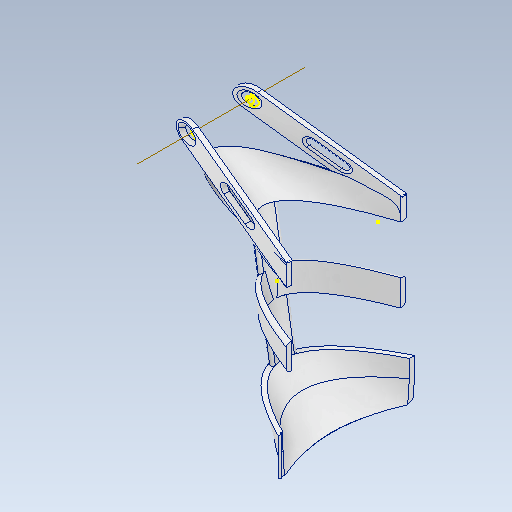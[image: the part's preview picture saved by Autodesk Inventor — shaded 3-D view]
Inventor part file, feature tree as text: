
AUTODESK INVENTOR PART (.ipt)
format: ipt  version: 2021 (Build 250183000, 183)  size: 1,121,280 bytes
history: native  units: mm
features: sketch x37, plane x11, other x4
ambient origin geometry x8: Origin, YZ Plane, XZ Plane, XY Plane, X Axis, Y Axis, Z Axis, Center Point
bodies: Solid1 (feature_tree)
feature tree (52):
  other  "Shoes (upper part).ipt"
  other  "Solid1::Shoes (upper part).ipt"
  other  "TaggingFeature1"
  sketch  "Sketch1"  dims[d0=10.0mm]
  sketch  "Sketch2"
  sketch  "Sketch3"
  sketch  "Sketch4"
  sketch  "Sketch5"
  sketch  "Sketch6"
  sketch  "Sketch7"
  sketch  "Sketch8"
  sketch  "Sketch9"
  sketch  "Sketch10"
  sketch  "Sketch11"
  sketch  "Sketch12"
  sketch  "Sketch13"
  sketch  "Sketch14"
  sketch  "Sketch15"
  sketch  "Sketch16"
  sketch  "Sketch17"
  sketch  "Sketch18"
  sketch  "Sketch19"
  sketch  "Sketch20"
  sketch  "Sketch21"
  sketch  "Sketch22"
  sketch  "Sketch23"
  sketch  "Sketch24"
  sketch  "Sketch25"
  sketch  "Sketch26"
  sketch  "Sketch27"
  sketch  "Sketch28"
  sketch  "Sketch29"
  sketch  "Sketch30"
  sketch  "Sketch31"
  sketch  "Sketch32"
  sketch  "Sketch33"
  sketch  "Sketch34"
  sketch  "Sketch35"
  sketch  "Sketch36"
  sketch  "3D Sketch1"
  plane  "Work Plane1"
  plane  "Work Plane2"
  plane  "Work Plane3"
  plane  "Work Plane4"
  plane  "Work Plane5"
  plane  "Work Plane6"
  plane  "Work Plane7"
  plane  "Work Plane8"
  plane  "Work Plane9"
  plane  "Work Plane10"
  plane  "Work Plane11"
  other  "Work Axis1"
